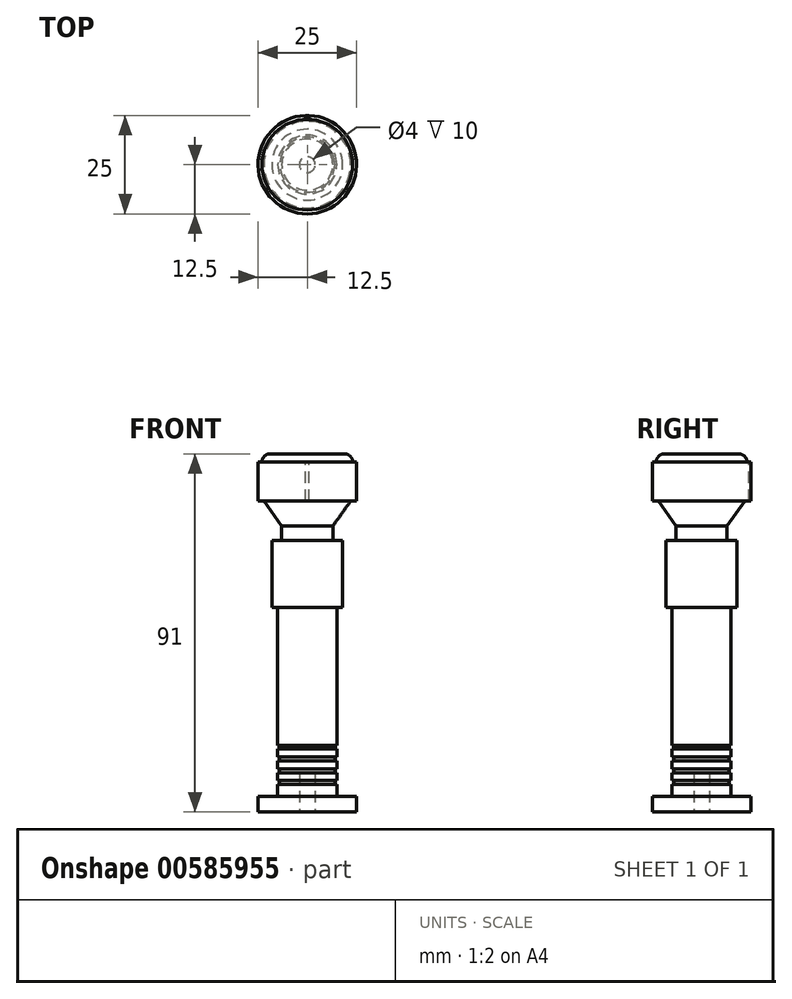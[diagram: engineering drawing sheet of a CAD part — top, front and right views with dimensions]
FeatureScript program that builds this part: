
annotation { "Feature Type Name" : "Feature", "Feature Type Description" : "" }
export const myFeature = defineFeature(function(context is Context, id is Id, definition is map)
    precondition{}
    {
        {
            var Q0;
            Q0=qCreatedBy(makeId("Top.planeOp"),FACE);
            var sketch = newSketch(context, id + "F0", { "sketchPlane" : qUnion([Q0])});
            skCircle(sketch, "E0", {"center": v(0, 0) * mm, "radius": 12.5 * mm});
            skSolve(sketch);
        }
        {
            var Q0;
            Q0 = qSketchRegion(id + "F0", true);
            extrude(context, id + "F1", {"entities" : qUnion([Q0]), "depth" : 4 * mm, "offsetDistance" : 25 * mm});
        }
        {
            var Q0;
            Q0=makeQuery(id+"F1.opExtrude","CAP_FACE",FACE,{"disambiguationData":[OSD([sQuery(id+"F0.wireOp",EDGE,"E0")])],"isStart":false});
            var sketch = newSketch(context, id + "F2", { "sketchPlane" : qUnion([Q0])});
            skCircle(sketch, "E1", {"center": v(0, 0) * mm, "radius": 7.5 * mm});
            skSolve(sketch);
        }
        {
            var Q0;
            Q0 = qSketchRegion(id + "F2", true);
            extrude(context, id + "F3", {"entities" : qUnion([Q0]), "operationType" : NewBodyOperationType.ADD, "depth" : 3 * mm, "offsetDistance" : 25 * mm});
        }
        {
            var Q0;
            Q0=makeQuery(id+"F3.opExtrude","CAP_FACE",FACE,{"disambiguationData":[OSD([sQuery(id+"F2.wireOp",EDGE,"E1")])],"isStart":false});
            var sketch = newSketch(context, id + "F4", { "sketchPlane" : qUnion([Q0])});
            skCircle(sketch, "E2", {"center": v(0, 0) * mm, "radius": 7 * mm});
            skSolve(sketch);
        }
        {
            var Q0;
            Q0 = qSketchRegion(id + "F4", true);
            extrude(context, id + "F5", {"entities" : qUnion([Q0]), "operationType" : NewBodyOperationType.ADD, "depth" : 1 * mm, "offsetDistance" : 25 * mm});
        }
        {
            var Q0;
            Q0=makeQuery(id+"F5.opExtrude","CAP_FACE",FACE,{"disambiguationData":[OSD([sQuery(id+"F4.wireOp",EDGE,"E2")])],"isStart":false});
            var sketch = newSketch(context, id + "F6", { "sketchPlane" : qUnion([Q0])});
            skCircle(sketch, "E3", {"center": v(0, 0) * mm, "radius": 7.5 * mm});
            skSolve(sketch);
        }
        {
            var Q0;
            Q0 = qSketchRegion(id + "F6", true);
            extrude(context, id + "F7", {"entities" : qUnion([Q0]), "operationType" : NewBodyOperationType.ADD, "depth" : 2 * mm, "offsetDistance" : 25 * mm});
        }
        {
            var Q0;
            Q0=makeQuery(id+"F7.opExtrude","CAP_FACE",FACE,{"disambiguationData":[OSD([sQuery(id+"F6.wireOp",EDGE,"E3")])],"isStart":false});
            var sketch = newSketch(context, id + "F8", { "sketchPlane" : qUnion([Q0])});
            skCircle(sketch, "E4", {"center": v(0, 0) * mm, "radius": 7 * mm});
            skSolve(sketch);
        }
        {
            var Q0;
            Q0 = qSketchRegion(id + "F8", true);
            extrude(context, id + "F9", {"entities" : qUnion([Q0]), "operationType" : NewBodyOperationType.ADD, "depth" : 1 * mm, "offsetDistance" : 25 * mm});
        }
        {
            var Q0;
            Q0=makeQuery(id+"F9.opExtrude","CAP_FACE",FACE,{"disambiguationData":[OSD([sQuery(id+"F8.wireOp",EDGE,"E4")])],"isStart":false});
            var sketch = newSketch(context, id + "F10", { "sketchPlane" : qUnion([Q0])});
            skCircle(sketch, "E5", {"center": v(0, 0) * mm, "radius": 7.5 * mm});
            skSolve(sketch);
        }
        {
            var Q0;
            Q0 = qSketchRegion(id + "F10", true);
            extrude(context, id + "F11", {"entities" : qUnion([Q0]), "operationType" : NewBodyOperationType.ADD, "depth" : 2 * mm, "offsetDistance" : 25 * mm});
        }
        {
            var Q0;
            Q0=makeQuery(id+"F11.opExtrude","CAP_FACE",FACE,{"disambiguationData":[OSD([sQuery(id+"F10.wireOp",EDGE,"E5")])],"isStart":false});
            var sketch = newSketch(context, id + "F12", { "sketchPlane" : qUnion([Q0])});
            skCircle(sketch, "E6", {"center": v(0, 0) * mm, "radius": 7 * mm});
            skSolve(sketch);
        }
        {
            var Q0;
            Q0 = qSketchRegion(id + "F12", true);
            extrude(context, id + "F13", {"entities" : qUnion([Q0]), "operationType" : NewBodyOperationType.ADD, "depth" : 1 * mm, "offsetDistance" : 25 * mm});
        }
        {
            var Q0;
            Q0=makeQuery(id+"F13.opExtrude","CAP_FACE",FACE,{"disambiguationData":[OSD([sQuery(id+"F12.wireOp",EDGE,"E6")])],"isStart":false});
            var sketch = newSketch(context, id + "F14", { "sketchPlane" : qUnion([Q0])});
            skCircle(sketch, "E7", {"center": v(0, 0) * mm, "radius": 7.5 * mm});
            skSolve(sketch);
        }
        {
            var Q0;
            Q0 = qSketchRegion(id + "F14", true);
            extrude(context, id + "F15", {"entities" : qUnion([Q0]), "operationType" : NewBodyOperationType.ADD, "depth" : 2 * mm, "offsetDistance" : 25 * mm});
        }
        {
            var Q0;
            Q0=makeQuery(id+"F15.opExtrude","CAP_FACE",FACE,{"disambiguationData":[OSD([sQuery(id+"F14.wireOp",EDGE,"E7")])],"isStart":false});
            var sketch = newSketch(context, id + "F16", { "sketchPlane" : qUnion([Q0])});
            skCircle(sketch, "E8", {"center": v(0, 0) * mm, "radius": 7 * mm});
            skSolve(sketch);
        }
        {
            var Q0;
            Q0 = qSketchRegion(id + "F16", true);
            extrude(context, id + "F17", {"entities" : qUnion([Q0]), "operationType" : NewBodyOperationType.ADD, "depth" : 1 * mm, "offsetDistance" : 25 * mm});
        }
        {
            var Q0;
            Q0=makeQuery(id+"F17.opExtrude","CAP_FACE",FACE,{"disambiguationData":[OSD([sQuery(id+"F16.wireOp",EDGE,"E8")])],"isStart":false});
            var sketch = newSketch(context, id + "F18", { "sketchPlane" : qUnion([Q0])});
            skCircle(sketch, "E9", {"center": v(0, 0) * mm, "radius": 7.5 * mm});
            skSolve(sketch);
        }
        {
            var Q0;
            Q0 = qSketchRegion(id + "F18", true);
            extrude(context, id + "F19", {"entities" : qUnion([Q0]), "operationType" : NewBodyOperationType.ADD, "depth" : 35 * mm, "offsetDistance" : 25 * mm});
        }
        {
            var Q0;
            Q0=makeQuery(id+"F19.opExtrude","CAP_FACE",FACE,{"disambiguationData":[OSD([sQuery(id+"F18.wireOp",EDGE,"E9")])],"isStart":false});
            var sketch = newSketch(context, id + "F20", { "sketchPlane" : qUnion([Q0])});
            skCircle(sketch, "E10", {"center": v(0, 0) * mm, "radius": 9 * mm});
            skSolve(sketch);
        }
        {
            var Q0;
            Q0 = qSketchRegion(id + "F20", true);
            extrude(context, id + "F21", {"entities" : qUnion([Q0]), "operationType" : NewBodyOperationType.ADD, "depth" : 17 * mm, "offsetDistance" : 25 * mm});
        }
        {
            var Q0;
            Q0=makeQuery(id+"F21.opExtrude","CAP_FACE",FACE,{"disambiguationData":[OSD([sQuery(id+"F20.wireOp",EDGE,"E10")])],"isStart":false});
            var sketch = newSketch(context, id + "F22", { "sketchPlane" : qUnion([Q0])});
            skCircle(sketch, "E11", {"center": v(0, 0) * mm, "radius": 6.5 * mm});
            skSolve(sketch);
        }
        {
            var Q0;
            Q0=makeQuery(id+"F22.imprint","IMPRINT",FACE,{"disambiguationData":[TD([[makeQuery(id+"F22.imprint","IMPRINT",EDGE,{"derivedFrom":sQuery(id+"F22.wireOp",EDGE,"E11")}),1.0]])]});
            extrude(context, id + "F23", {"entities" : qUnion([Q0]), "operationType" : NewBodyOperationType.ADD, "depth" : 3 * mm, "offsetDistance" : 25 * mm});
        }
        {
            var Q0;
            Q0=makeQuery(id+"F23.opExtrude","CAP_FACE",FACE,{"disambiguationData":[OSD([sQuery(id+"F22.wireOp",EDGE,"E11")])],"isStart":false});
            var sketch = newSketch(context, id + "F24", { "sketchPlane" : qUnion([Q0])});
            skCircle(sketch, "E12", {"center": v(0, 0) * mm, "radius": 11 * mm});
            skSolve(sketch);
        }
        {
            var Q0;
            Q0 = qSketchRegion(id + "F24", true);
            extrude(context, id + "F25", {"entities" : qUnion([Q0]), "operationType" : NewBodyOperationType.ADD, "depth" : 7 * mm, "offsetDistance" : 25 * mm});
        }
        {
            var Q0;
            Q0=makeQuery(id+"F25.opExtrude","CAP_FACE",FACE,{"disambiguationData":[OSD([sQuery(id+"F24.wireOp",EDGE,"E12")])],"isStart":false});
            var sketch = newSketch(context, id + "F26", { "sketchPlane" : qUnion([Q0])});
            skCircle(sketch, "E13", {"center": v(0, 0) * mm, "radius": 12.5 * mm});
            skSolve(sketch);
        }
        {
            var Q0;
            Q0 = qSketchRegion(id + "F26", true);
            extrude(context, id + "F27", {"entities" : qUnion([Q0]), "operationType" : NewBodyOperationType.ADD, "depth" : 10 * mm, "offsetDistance" : 25 * mm});
        }
        {
            var Q0;
            Q0=makeQuery(id+"F25.opExtrude","CAP_EDGE",EDGE,{"disambiguationData":[OSD([sQuery(id+"F24.wireOp",EDGE,"E12")])],"isStart":true});
            chamfer(context, id + "F28", {"entities" : qUnion([Q0]), "chamferType" : ChamferType.TWO_OFFSETS, "width1" : 7 * mm, "oppositeDirection" : false, "width2" : 5 * mm, "tangentPropagation" : true});
        }
        {
            var Q0;
            Q0=makeQuery(id+"F27.opExtrude","CAP_FACE",FACE,{"disambiguationData":[OSD([sQuery(id+"F26.wireOp",EDGE,"E13")])],"isStart":false});
            var sketch = newSketch(context, id + "F29", { "sketchPlane" : qUnion([Q0])});
            skCircle(sketch, "E14", {"center": v(0, 0) * mm, "radius": 11.5 * mm});
            skSolve(sketch);
        }
        {
            var Q0;
            Q0=makeQuery(id+"F29.imprint","IMPRINT",FACE,{"disambiguationData":[TD([[makeQuery(id+"F29.imprint","IMPRINT",EDGE,{"derivedFrom":sQuery(id+"F29.wireOp",EDGE,"E14")}),1.0]])]});
            extrude(context, id + "F30", {"entities" : qUnion([Q0]), "operationType" : NewBodyOperationType.ADD, "depth" : 2 * mm, "offsetDistance" : 25 * mm});
        }
        {
            var Q0;
            Q0=makeQuery(id+"F30.opExtrude","CAP_EDGE",EDGE,{"disambiguationData":[OSD([sQuery(id+"F29.wireOp",EDGE,"E14")])],"isStart":false});
            fillet(context, id + "F31", {"entities" : qUnion([Q0]), "radius" : 2 * mm, "tangentPropagation" : true, "allowEdgeOverflow" : false});
        }
        {
            var Q0;
            Q0=makeQuery(id+"F27.opExtrude","CAP_FACE",FACE,{"disambiguationData":[OSD([sQuery(id+"F26.wireOp",EDGE,"E13")])],"isStart":false});
            var sketch = newSketch(context, id + "F32", { "sketchPlane" : qUnion([Q0])});
            skLineSegment(sketch, "E15.bottom", {"start": v(-0.5, 13) * mm, "end": v(0.5, 13) * mm});
            skLineSegment(sketch, "E15.top", {"start": v(-0.5, 12) * mm, "end": v(0.5, 12) * mm});
            skLineSegment(sketch, "E15.left", {"start": v(-0.5, 13) * mm, "end": v(-0.5, 12) * mm});
            skLineSegment(sketch, "E15.right", {"start": v(0.5, 13) * mm, "end": v(0.5, 12) * mm});
            skPoint(sketch, "E15.middle", {"position": v(0, 12.5) * mm});
            skSolve(sketch);
        }
        {
            var Q0;
            {var subQ0=sQuery(id+"F32.wireOp",EDGE,"E15.top");Q0=makeQuery(id+"F32.imprint","IMPRINT",FACE,{"disambiguationData":[TD([[makeQuery(id+"F32.imprint","IMPRINT",EDGE,{"derivedFrom":subQ0}),1.0]])]});}
            extrude(context, id + "F33", {"entities" : qUnion([Q0]), "operationType" : NewBodyOperationType.REMOVE, "oppositeDirection" : true, "depth" : 25 * mm, "offsetDistance" : 25 * mm});
        }
        {
            var Q0;
            Q0=makeQuery(id+"F1.opExtrude","CAP_FACE",FACE,{"disambiguationData":[OSD([sQuery(id+"F0.wireOp",EDGE,"E0")])],"isStart":true});
            var sketch = newSketch(context, id + "F34", { "sketchPlane" : qUnion([Q0])});
            skCircle(sketch, "E16", {"center": v(0, 0) * mm, "radius": 2 * mm});
            skSolve(sketch);
        }
        {
            var Q0;
            Q0=makeQuery(id+"F34.imprint","IMPRINT",FACE,{"disambiguationData":[TD([[makeQuery(id+"F34.imprint","IMPRINT",EDGE,{"derivedFrom":sQuery(id+"F34.wireOp",EDGE,"E16")}),1.0]])]});
            extrude(context, id + "F35", {"entities" : qUnion([Q0]), "operationType" : NewBodyOperationType.REMOVE, "oppositeDirection" : true, "depth" : 10 * mm, "offsetDistance" : 25 * mm});
        }
    });
